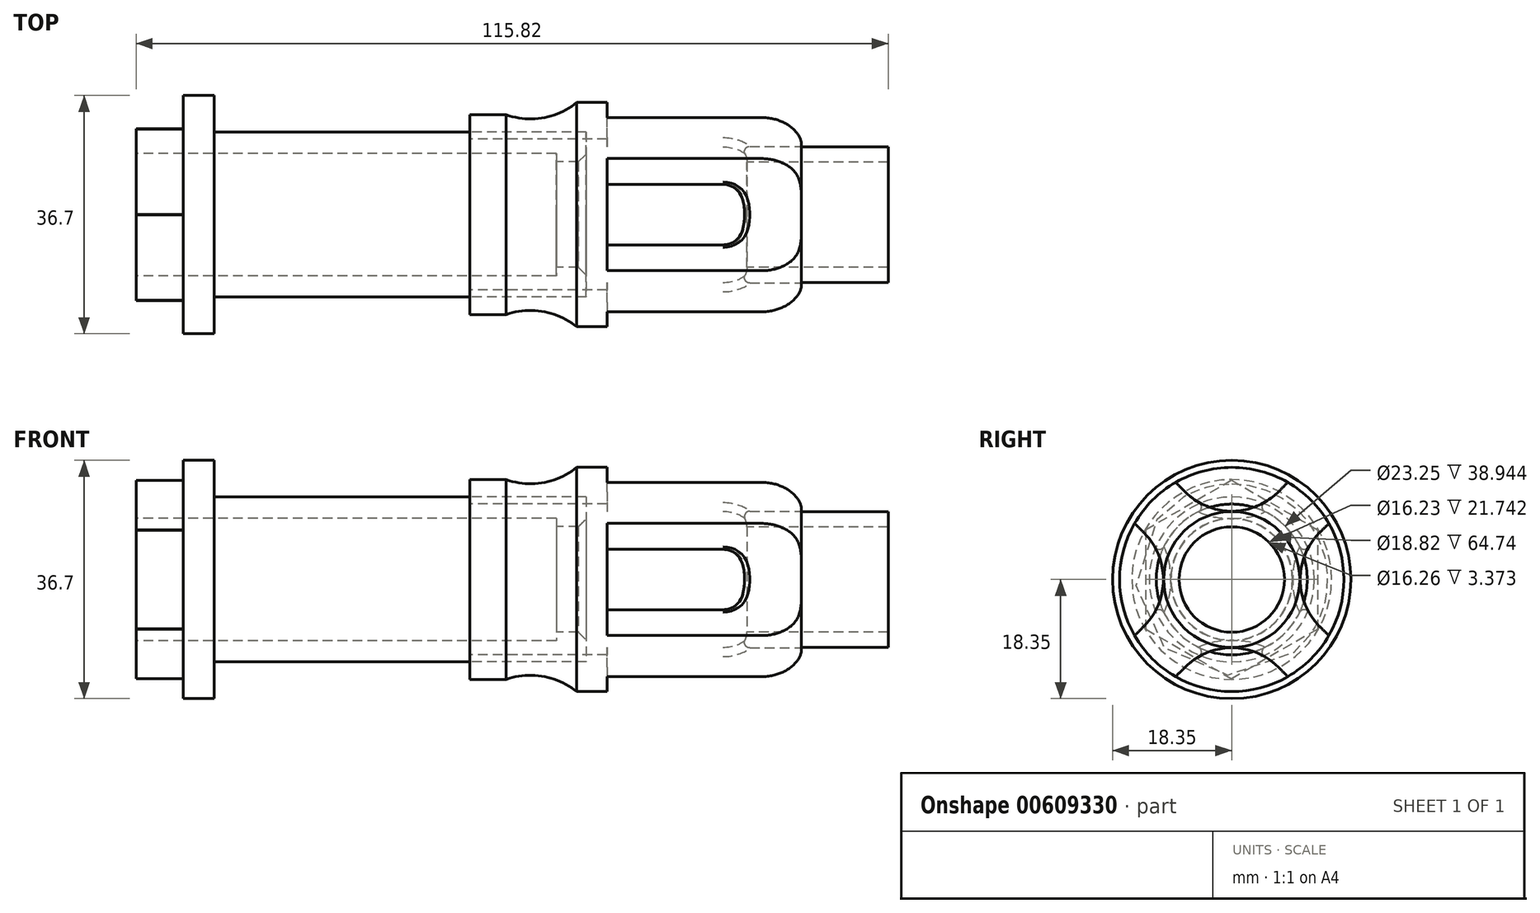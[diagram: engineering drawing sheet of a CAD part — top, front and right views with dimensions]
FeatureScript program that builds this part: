
annotation { "Feature Type Name" : "Feature", "Feature Type Description" : "" }
export const myFeature = defineFeature(function(context is Context, id is Id, definition is map)
    precondition{}
    {
        {
            var Q0;
            Q0=qCreatedBy(makeId("Top.planeOp"),FACE);
            var sketch = newSketch(context, id + "F0", { "sketchPlane" : qUnion([Q0])});
            skLineSegment(sketch, "E0", {"start": v(0, 0) * mm, "end": v(86.66, 0) * mm, "construction": true});
            skLineSegment(sketch, "E1", {"start": v(0, 19.08) * mm, "end": v(9.07, 19.08) * mm});
            skLineSegment(sketch, "E2", {"start": v(0, 19.08) * mm, "end": v(0, 11.76) * mm});
            skLineSegment(sketch, "E3", {"start": v(0, 11.76) * mm, "end": v(80.92, 11.76) * mm});
            skLineSegment(sketch, "E4", {"start": v(9.07, 19.08) * mm, "end": v(9.07, 22.94) * mm});
            skLineSegment(sketch, "E5", {"start": v(9.07, 22.94) * mm, "end": v(15.06, 22.94) * mm});
            skLineSegment(sketch, "E6", {"start": v(15.06, 22.94) * mm, "end": v(15.06, 15.87) * mm});
            skLineSegment(sketch, "E7", {"start": v(15.06, 15.87) * mm, "end": v(86.66, 15.88) * mm});
            skLineSegment(sketch, "E8", {"start": v(80.92, 10.16) * mm, "end": v(85.14, 10.16) * mm});
            skLineSegment(sketch, "E9", {"start": v(86.66, 15.88) * mm, "end": v(86.66, 11.68) * mm});
            skLineSegment(sketch, "E10", {"start": v(80.92, 10.16) * mm, "end": v(80.92, 11.76) * mm});
            skLineSegment(sketch, "E11", {"start": v(86.66, 11.68) * mm, "end": v(85.14, 10.16) * mm});
            skPoint(sketch, "E12.orphan", {"position": v(86.66, 10.16) * mm});
            skSolve(sketch);
        }
        {
            var Q0;
            Q0=makeQuery(id+"F0.imprint","IMPRINT",FACE,{"disambiguationData":[TD([[makeQuery(id+"F0.imprint","IMPRINT",EDGE,{"derivedFrom":sQuery(id+"F0.wireOp",EDGE,"E1")}),-1.0]])]});
            var Q1;
            Q1=sQuery(id+"F0.wireOp",EDGE,"E0");
            revolve(context, id + "F1", {"entities" : qUnion([Q0]), "axis" : qUnion([Q1]), "revolveType" : RevolveType.FULL});
        }
        {
            var Q0;
            Q0=qCreatedBy(makeId("Right.planeOp"),FACE);
            var sketch = newSketch(context, id + "F2", { "sketchPlane" : qUnion([Q0])});
            skCircle(sketch, "E13", {"center": v(0, 0) * mm, "radius": 19.1 * mm, "construction": true});
            skLineSegment(sketch, "E14", {"start": v(0, 0) * mm, "end": v(0, 19.1) * mm, "construction": true});
            skLineSegment(sketch, "E15", {"start": v(0, 19.1) * mm, "end": v(-16.54, 9.55) * mm});
            skLineSegment(sketch, "E16", {"start": v(-16.54, 9.55) * mm, "end": v(-16.54, -9.55) * mm});
            skLineSegment(sketch, "E17", {"start": v(-16.54, -9.55) * mm, "end": v(0, -19.1) * mm});
            skLineSegment(sketch, "E18.MirrorCS", {"start": v(0, 19.1) * mm, "end": v(16.54, 9.55) * mm});
            skLineSegment(sketch, "E19.MirrorCS", {"start": v(16.54, 9.55) * mm, "end": v(16.54, -9.55) * mm});
            skLineSegment(sketch, "E20.MirrorCS", {"start": v(16.54, -9.55) * mm, "end": v(0, -19.1) * mm});
            skCircle(sketch, "E21", {"center": v(-0.66, 0) * mm, "radius": 26.06 * mm});
            skSolve(sketch);
        }
        {
            var Q0;
            Q0=makeQuery(id+"F2.imprint","IMPRINT",FACE,{"disambiguationData":[TD([[makeQuery(id+"F2.imprint","IMPRINT",EDGE,{"derivedFrom":sQuery(id+"F2.wireOp",EDGE,"E15")}),-1.0]])]});
            extrude(context, id + "F3", {"entities" : qUnion([Q0]), "operationType" : NewBodyOperationType.REMOVE, "depth" : 9.07 * mm, "offsetDistance" : 25.4 * mm});
        }
        {
            var Q0;
            Q0=qCreatedBy(makeId("Top.planeOp"),FACE);
            var sketch = newSketch(context, id + "F4", { "sketchPlane" : qUnion([Q0])});
            skLineSegment(sketch, "E22", {"start": v(64.26, 14.53) * mm, "end": v(112.94, 14.53) * mm});
            skLineSegment(sketch, "E23", {"start": v(64.26, 14.53) * mm, "end": v(64.26, 19.23) * mm});
            skLineSegment(sketch, "E24", {"start": v(64.26, 19.23) * mm, "end": v(71.25, 19.23) * mm});
            skLineSegment(sketch, "E25", {"start": v(0, 0) * mm, "end": v(144.78, 0) * mm, "construction": true});
            skArc(sketch, "E26", {"start": v(71.25, 19.23) * mm, "mid": v(78.35, 18.65) * mm, "end": v(84.84, 21.59) * mm});
            skLineSegment(sketch, "E27", {"start": v(84.84, 21.59) * mm, "end": v(120.42, 21.59) * mm});
            skArc(sketch, "E28", {"start": v(128.04, 13.08) * mm, "mid": v(126.13, 19.04) * mm, "end": v(120.42, 21.59) * mm});
            skLineSegment(sketch, "E29", {"start": v(128.04, 13.08) * mm, "end": v(144.78, 13.08) * mm});
            skLineSegment(sketch, "E30", {"start": v(144.78, 13.08) * mm, "end": v(144.78, 10.14) * mm});
            skLineSegment(sketch, "E31", {"start": v(144.78, 10.14) * mm, "end": v(117.6, 10.14) * mm});
            skArc(sketch, "E32", {"start": v(117.6, 10.14) * mm, "mid": v(116.14, 13.26) * mm, "end": v(112.94, 14.53) * mm});
            skSolve(sketch);
        }
        {
            var Q0;
            Q0=makeQuery(id+"F4.imprint","IMPRINT",FACE,{"disambiguationData":[TD([[makeQuery(id+"F4.imprint","IMPRINT",EDGE,{"derivedFrom":sQuery(id+"F4.wireOp",EDGE,"E22")}),1.0]])]});
            var Q1;
            Q1=sQuery(id+"F4.wireOp",EDGE,"E25");
            revolve(context, id + "F5", {"entities" : qUnion([Q0]), "axis" : qUnion([Q1]), "revolveType" : RevolveType.FULL});
        }
        {
            var Q0;
            Q0=makeQuery(id+"F5.opRevolve","SWEPT_FACE",FACE,{"disambiguationData":[OSD([sQuery(id+"F4.wireOp",EDGE,"E30")])]});
            var sketch = newSketch(context, id + "F6", { "sketchPlane" : qUnion([Q0])});
            skLineSegment(sketch, "E33", {"start": v(0, 0) * mm, "end": v(0, 25.86) * mm, "construction": true});
            skArc(sketch, "E34", {"start": v(-8.98, 16.88) * mm, "mid": v(-4.86, 14.13) * mm, "end": v(0, 13.16) * mm});
            skLineSegment(sketch, "E35", {"start": v(-8.98, 16.88) * mm, "end": v(-19.05, 26.95) * mm});
            skLineSegment(sketch, "E36", {"start": v(-19.05, 26.95) * mm, "end": v(0, 26.95) * mm});
            skLineSegment(sketch, "E37.MirrorCS", {"start": v(19.05, 26.95) * mm, "end": v(0, 26.95) * mm});
            skLineSegment(sketch, "E38.MirrorCS", {"start": v(8.98, 16.88) * mm, "end": v(19.05, 26.95) * mm});
            skArc(sketch, "E39.MirrorCS", {"start": v(8.98, 16.88) * mm, "mid": v(4.86, 14.13) * mm, "end": v(0, 13.16) * mm});
            skArc(sketch, "E40", {"start": v(10.8, 18.7) * mm, "mid": v(0, 21.59) * mm, "end": v(-10.8, 18.7) * mm, "construction": true});
            skPoint(sketch, "E41", {"position": v(0, 21.59) * mm});
            skLineSegment(sketch, "E42", {"start": v(0, 0) * mm, "end": v(30.1, 0) * mm, "construction": true});
            skLineSegment(sketch, "E43.MirrorCS", {"start": v(8.98, -16.88) * mm, "end": v(19.05, -26.95) * mm});
            skLineSegment(sketch, "E44.MirrorCS", {"start": v(19.05, -26.95) * mm, "end": v(0, -26.95) * mm});
            skLineSegment(sketch, "E45.MirrorCS", {"start": v(-19.05, -26.95) * mm, "end": v(0, -26.95) * mm});
            skLineSegment(sketch, "E46.MirrorCS", {"start": v(-8.98, -16.88) * mm, "end": v(-19.05, -26.95) * mm});
            skArc(sketch, "E47.MirrorCS", {"start": v(-8.98, -16.88) * mm, "mid": v(-4.86, -14.13) * mm, "end": v(0, -13.16) * mm});
            skArc(sketch, "E48.MirrorCS", {"start": v(8.98, -16.88) * mm, "mid": v(4.86, -14.13) * mm, "end": v(0, -13.16) * mm});
            skLineSegment(sketch, "E49", {"start": v(0, 0) * mm, "end": v(-46, 46) * mm, "construction": true});
            skLineSegment(sketch, "E50.MirrorCS", {"start": v(-16.88, 8.98) * mm, "end": v(-26.95, 19.05) * mm});
            skLineSegment(sketch, "E51.MirrorCS", {"start": v(-26.95, 19.05) * mm, "end": v(-26.95, 0) * mm});
            skLineSegment(sketch, "E52.MirrorCS", {"start": v(-26.95, -19.05) * mm, "end": v(-26.95, 0) * mm});
            skLineSegment(sketch, "E53.MirrorCS", {"start": v(-16.88, -8.98) * mm, "end": v(-26.95, -19.05) * mm});
            skArc(sketch, "E54.MirrorCS", {"start": v(-16.88, -8.98) * mm, "mid": v(-14.13, -4.86) * mm, "end": v(-13.16, 0) * mm});
            skArc(sketch, "E55.MirrorCS", {"start": v(-16.88, 8.98) * mm, "mid": v(-14.13, 4.86) * mm, "end": v(-13.16, 0) * mm});
            skLineSegment(sketch, "E56", {"start": v(0, 0) * mm, "end": v(31.33, 31.33) * mm, "construction": true});
            skLineSegment(sketch, "E57.MirrorCS", {"start": v(16.88, 8.98) * mm, "end": v(26.95, 19.05) * mm});
            skLineSegment(sketch, "E58.MirrorCS", {"start": v(26.95, 19.05) * mm, "end": v(26.95, 0) * mm});
            skLineSegment(sketch, "E59.MirrorCS", {"start": v(26.95, -19.05) * mm, "end": v(26.95, 0) * mm});
            skLineSegment(sketch, "E60.MirrorCS", {"start": v(16.88, -8.98) * mm, "end": v(26.95, -19.05) * mm});
            skArc(sketch, "E61.MirrorCS", {"start": v(16.88, -8.98) * mm, "mid": v(14.13, -4.86) * mm, "end": v(13.16, 0) * mm});
            skArc(sketch, "E62.MirrorCS", {"start": v(16.88, 8.98) * mm, "mid": v(14.13, 4.86) * mm, "end": v(13.16, 0) * mm});
            skSolve(sketch);
        }
        {
            var Q0;
            Q0=makeQuery(id+"F6.imprint","IMPRINT",FACE,{"disambiguationData":[TD([[makeQuery(id+"F6.imprint","IMPRINT",EDGE,{"derivedFrom":sQuery(id+"F6.wireOp",EDGE,"E34")}),1.0]])]});
            var Q1;
            Q1=makeQuery(id+"F6.imprint","IMPRINT",FACE,{"disambiguationData":[TD([[makeQuery(id+"F6.imprint","IMPRINT",EDGE,{"derivedFrom":sQuery(id+"F6.wireOp",EDGE,"E51.MirrorCS")}),1.0]])]});
            var Q2;
            Q2=makeQuery(id+"F6.imprint","IMPRINT",FACE,{"disambiguationData":[TD([[makeQuery(id+"F6.imprint","IMPRINT",EDGE,{"derivedFrom":sQuery(id+"F6.wireOp",EDGE,"E43.MirrorCS")}),-1.0]])]});
            var Q3;
            Q3=makeQuery(id+"F6.imprint","IMPRINT",FACE,{"disambiguationData":[TD([[makeQuery(id+"F6.imprint","IMPRINT",EDGE,{"derivedFrom":sQuery(id+"F6.wireOp",EDGE,"E57.MirrorCS")}),-1.0]])]});
            extrude(context, id + "F7", {"entities" : qUnion([Q0, Q1, Q2, Q3]), "operationType" : NewBodyOperationType.REMOVE, "oppositeDirection" : true, "depth" : 54.1 * mm, "offsetDistance" : 25.4 * mm});
        }
        {
            var Q0;
            Q0=makeQuery(id+"F7.boolean.opBoolean","INTERSECT",EDGE,{"disambiguationData":[OD(0.0)],"derivedFrom":[makeQuery(id+"F5.opRevolve","SWEPT_FACE",FACE,{"disambiguationData":[OSD([sQuery(id+"F4.wireOp",EDGE,"E22")])]}),makeQuery(id+"F7.opExtrude","SWEPT_FACE",FACE,{"disambiguationData":[OSD([sQuery(id+"F6.wireOp",EDGE,"E34"),sQuery(id+"F6.wireOp",EDGE,"E39.MirrorCS")])]})]});
            var Q1;
            Q1=makeQuery(id+"F7.boolean.opBoolean","INTERSECT",EDGE,{"disambiguationData":[OD(1.0)],"derivedFrom":[makeQuery(id+"F5.opRevolve","SWEPT_FACE",FACE,{"disambiguationData":[OSD([sQuery(id+"F4.wireOp",EDGE,"E22")])]}),makeQuery(id+"F7.opExtrude","SWEPT_FACE",FACE,{"disambiguationData":[OSD([sQuery(id+"F6.wireOp",EDGE,"E61.MirrorCS"),sQuery(id+"F6.wireOp",EDGE,"E62.MirrorCS")])]})]});
            var Q2;
            Q2=makeQuery(id+"F7.boolean.opBoolean","INTERSECT",EDGE,{"disambiguationData":[OD(0.0)],"derivedFrom":[makeQuery(id+"F5.opRevolve","SWEPT_FACE",FACE,{"disambiguationData":[OSD([sQuery(id+"F4.wireOp",EDGE,"E22")])]}),makeQuery(id+"F7.opExtrude","SWEPT_FACE",FACE,{"disambiguationData":[OSD([sQuery(id+"F6.wireOp",EDGE,"E47.MirrorCS"),sQuery(id+"F6.wireOp",EDGE,"E48.MirrorCS")])]})]});
            var Q3;
            Q3=makeQuery(id+"F7.boolean.opBoolean","INTERSECT",EDGE,{"disambiguationData":[OD(1.0)],"derivedFrom":[makeQuery(id+"F5.opRevolve","SWEPT_FACE",FACE,{"disambiguationData":[OSD([sQuery(id+"F4.wireOp",EDGE,"E22")])]}),makeQuery(id+"F7.opExtrude","SWEPT_FACE",FACE,{"disambiguationData":[OSD([sQuery(id+"F6.wireOp",EDGE,"E54.MirrorCS"),sQuery(id+"F6.wireOp",EDGE,"E55.MirrorCS")])]})]});
            fillet(context, id + "F8", {"entities" : qUnion([Q0, Q1, Q2, Q3]), "radius" : 1.02 * mm, "tangentPropagation" : true, "allowEdgeOverflow" : false});
        }
        {
            var Q0;
            Q0=makeQuery(id+"F1.opRevolve","SWEPT_BODY",BODY,{"disambiguationData":[OSD([sQuery(id+"F0.wireOp",EDGE,"E1"),sQuery(id+"F0.wireOp",EDGE,"E2"),sQuery(id+"F0.wireOp",EDGE,"E3"),sQuery(id+"F0.wireOp",EDGE,"E4"),sQuery(id+"F0.wireOp",EDGE,"E5"),sQuery(id+"F0.wireOp",EDGE,"E6"),sQuery(id+"F0.wireOp",EDGE,"E7"),sQuery(id+"F0.wireOp",EDGE,"E8"),sQuery(id+"F0.wireOp",EDGE,"E9"),sQuery(id+"F0.wireOp",EDGE,"E10"),sQuery(id+"F0.wireOp",EDGE,"E11")])]});
            var Q1;
            Q1=qCreatedBy(makeId("Origin.pointOp"),VERTEX);
            transform(context, id + "F9", {"entities" : qUnion([Q0]), "transformType" : TransformType.SCALE_UNIFORMLY, "scale" : .8, "scalePoint" : qUnion([Q1]), "makeCopy" : false});
        }
        {
            var Q0;
            Q0=makeQuery(id+"F5.opRevolve","SWEPT_BODY",BODY,{"disambiguationData":[OSD([sQuery(id+"F4.wireOp",EDGE,"E22"),sQuery(id+"F4.wireOp",EDGE,"E23"),sQuery(id+"F4.wireOp",EDGE,"E24"),sQuery(id+"F4.wireOp",EDGE,"E26"),sQuery(id+"F4.wireOp",EDGE,"E27"),sQuery(id+"F4.wireOp",EDGE,"E28"),sQuery(id+"F4.wireOp",EDGE,"E29"),sQuery(id+"F4.wireOp",EDGE,"E30"),sQuery(id+"F4.wireOp",EDGE,"E31"),sQuery(id+"F4.wireOp",EDGE,"E32")])]});
            var Q1;
            Q1=qCreatedBy(makeId("Origin.pointOp"),VERTEX);
            transform(context, id + "F10", {"entities" : qUnion([Q0]), "transformType" : TransformType.SCALE_UNIFORMLY, "scale" : .8, "scalePoint" : qUnion([Q1]), "makeCopy" : false});
        }
    });
